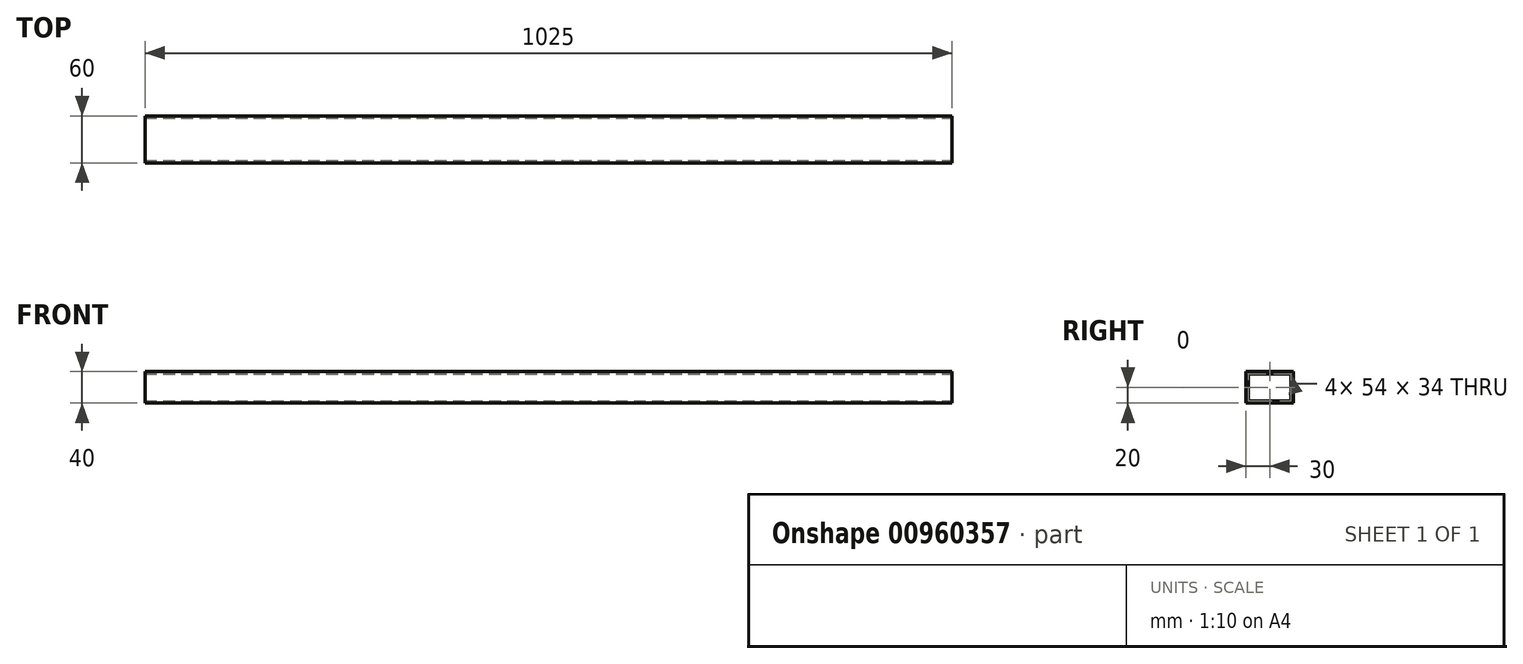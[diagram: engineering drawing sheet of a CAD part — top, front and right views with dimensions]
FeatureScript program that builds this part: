
annotation { "Feature Type Name" : "Feature", "Feature Type Description" : "" }
export const myFeature = defineFeature(function(context is Context, id is Id, definition is map)
    precondition{}
    {
        {
            var Q0;
            Q0=qCreatedBy(makeId("Top.planeOp"),FACE);
            var sketch = newSketch(context, id + "F0", { "sketchPlane" : qUnion([Q0])});
            skLineSegment(sketch, "E0.bottom", {"start": v(-512.5, 30) * mm, "end": v(512.5, 30) * mm});
            skLineSegment(sketch, "E0.top", {"start": v(-512.5, -30) * mm, "end": v(512.5, -30) * mm});
            skLineSegment(sketch, "E0.left", {"start": v(-512.5, 30) * mm, "end": v(-512.5, -30) * mm});
            skLineSegment(sketch, "E0.right", {"start": v(512.5, 30) * mm, "end": v(512.5, -30) * mm});
            skPoint(sketch, "E0.middle", {"position": v(0, 0) * mm});
            skSolve(sketch);
        }
        {
            var Q0;
            Q0=qSketchRegion(id+"F0",true);
            extrude(context, id + "F1", {"entities" : qUnion([Q0]), "depth" : 40 * mm, "offsetDistance" : 25 * mm});
        }
        {
            var Q0;
            Q0=makeQuery(id+"F1.opExtrude","SWEPT_FACE",FACE,{"disambiguationData":[OSD([sQuery(id+"F0.wireOp",EDGE,"E0.left")])]});
            var Q1;
            Q1=makeQuery(id+"F1.opExtrude","SWEPT_FACE",FACE,{"disambiguationData":[OSD([sQuery(id+"F0.wireOp",EDGE,"E0.right")])]});
            shell(context, id + "F2", {"entities" : qUnion([Q0, Q1]), "thickness" : 3 * mm});
        }
    });
